# Revit family: QF_KOLDBOX_KBC1_240315125633
name_source: partatom
category: Specialty Equipment
units: mm (PartAtom-declared; Revit-internal decimal feet)

## family parameters
Always vertical = Yes
Cut with Voids When Loaded = No
OmniClass Number = 23.40.40.14
OmniClass Title = Food Service Equipment
Part Type = Normal
Room Calculation Point = No
Round Connector Dimension = Use Diameter
Shared = No
Work Plane-Based = No

## types (1)
- KBC1
    Cold Water Consumption = 0.0 L/s
    Cost = 554 $
    Default Elevation = 0 mm  [stored 0 ft]
    Description = KOLDBOX SINGLE DOOR BACK BAR COOLER
    Direct Heat Output = 0 W
    Filtered Water Flow = 0.0 L/s
    Filtered Water Maximum Pressure = 0.0 Pa
    Filtered Water Minimum Pressure = 0.0 Pa
    Filtered Water Supply Size = 0 mm
    Gas power kW = 0
    Hot Water Consumption = 0.0 L/s
    Latent Heat Output = 0 W
    Manufacturer = KOLDBOX
    Model = KBC1
    National Water Regulation Certification = No
    Odor Trap Included = No
    Refrigeration Liquid Line Size = 0 mm  [stored 0 ft]
    Refrigeration Suction Line Size = 0 mm  [stored 0 ft]
    Sensitive Heat Output = 0 W
    Treated Water Flow = 0.0 L/s
    Treated Water Maximum Pressure = 0.0 Pa
    Treated Water Minimum Pressure = 0.0 Pa
    Treated Water Recommended Temperature = 0 °C
    Treated Water Size = 0 mm
    URL = www.koldbox.com

note: [stored X ft] marks values corroborated as IEEE doubles in the binary element streams (Revit-internal decimal feet)

## geometry (parser evidence)
native form markers: Sweep x5
no freeform markers — native parametric forms only
